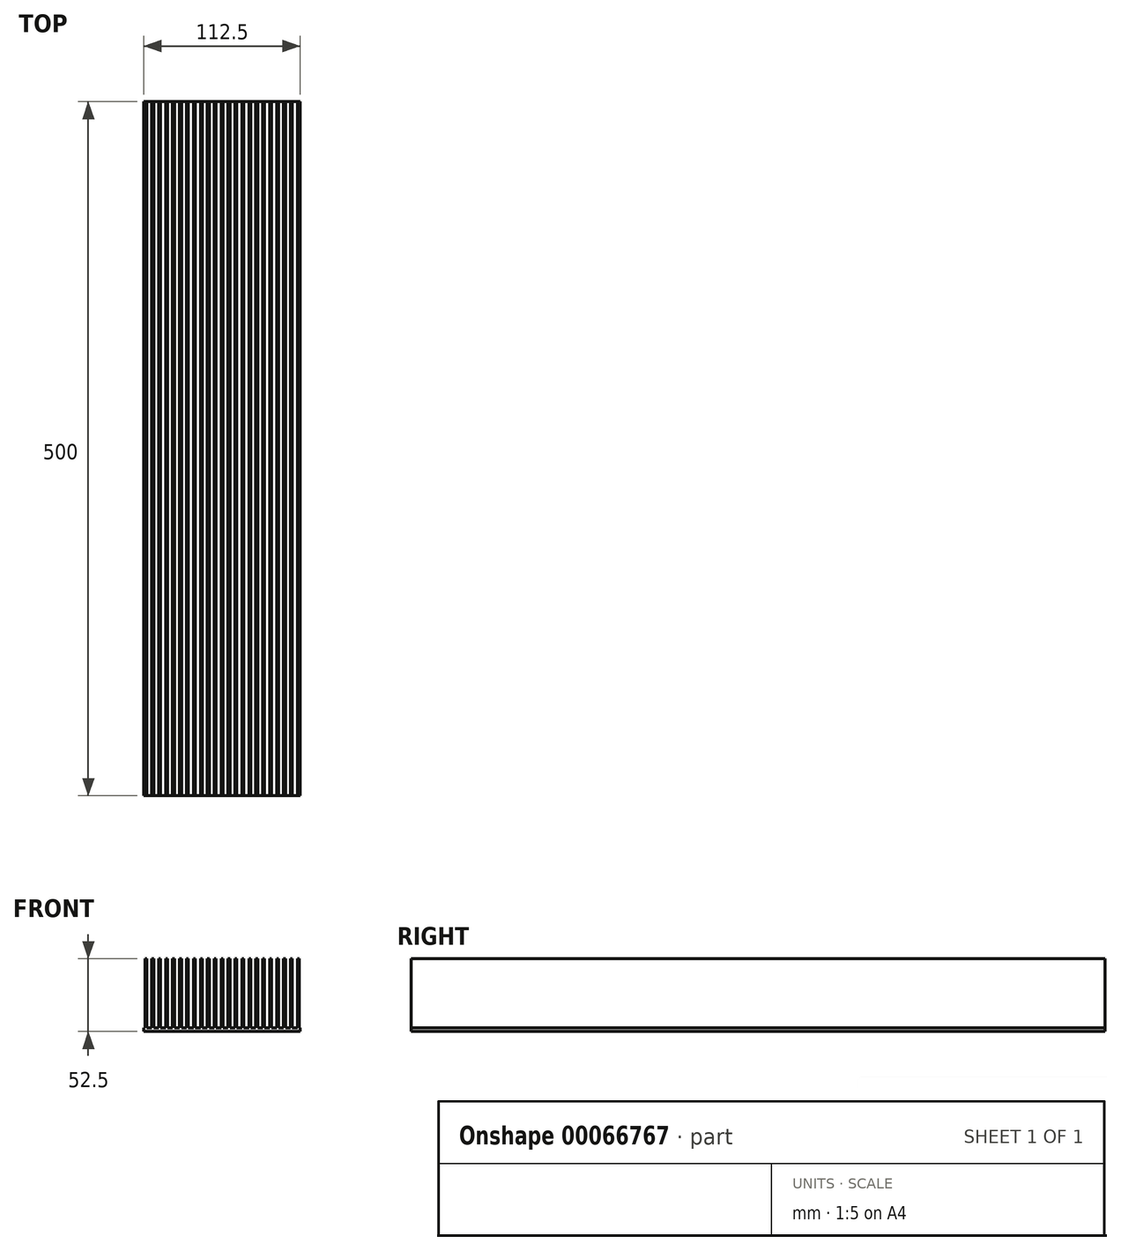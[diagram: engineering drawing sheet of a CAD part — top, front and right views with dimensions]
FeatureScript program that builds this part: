
annotation { "Feature Type Name" : "Feature", "Feature Type Description" : "" }
export const myFeature = defineFeature(function(context is Context, id is Id, definition is map)
    precondition{}
    {
        {
            var Q0;
            Q0=qCreatedBy(makeId("Front.planeOp"),FACE);
            var sketch = newSketch(context, id + "F0", { "sketchPlane" : qUnion([Q0])});
            skLineSegment(sketch, "E0", {"start": v(56.25, 1) * mm, "end": v(56.25, 3.5) * mm});
            skLineSegment(sketch, "E1", {"start": v(56.25, 3.5) * mm, "end": v(55.75, 3.5) * mm});
            skLineSegment(sketch, "E2", {"start": v(55.75, 3.5) * mm, "end": v(55.75, 53.5) * mm});
            skLineSegment(sketch, "E3", {"start": v(55.75, 53.5) * mm, "end": v(54.4, 53.5) * mm});
            skLineSegment(sketch, "E4", {"start": v(54.4, 53.5) * mm, "end": v(54.4, 3.5) * mm});
            skLineSegment(sketch, "E5", {"start": v(0, 1) * mm, "end": v(-56.25, 1) * mm});
            skLineSegment(sketch, "E6", {"start": v(-56.25, 1) * mm, "end": v(-56.25, 3.5) * mm});
            skLineSegment(sketch, "E7", {"start": v(-56.25, 3.5) * mm, "end": v(-52.25, 3.5) * mm});
            skLineSegment(sketch, "E8", {"start": v(-52.25, 3.5) * mm, "end": v(-52.25, 55.1) * mm, "construction": true});
            skLineSegment(sketch, "E9", {"start": v(-52.25, 3.5) * mm, "end": v(54.4, 3.5) * mm});
            skLineSegment(sketch, "E10.1.0.0", {"start": v(50.75, 53.5) * mm, "end": v(49.4, 53.5) * mm});
            skLineSegment(sketch, "E10.1.0.1", {"start": v(50.75, 3.5) * mm, "end": v(50.75, 53.5) * mm});
            skLineSegment(sketch, "E10.1.0.2", {"start": v(49.4, 53.5) * mm, "end": v(49.4, 3.5) * mm});
            skLineSegment(sketch, "E10.2.0.0", {"start": v(45.75, 53.5) * mm, "end": v(44.4, 53.5) * mm});
            skLineSegment(sketch, "E10.2.0.1", {"start": v(45.75, 3.5) * mm, "end": v(45.75, 53.5) * mm});
            skLineSegment(sketch, "E10.2.0.2", {"start": v(44.4, 53.5) * mm, "end": v(44.4, 3.5) * mm});
            skLineSegment(sketch, "E10.3.0.0", {"start": v(40.75, 53.5) * mm, "end": v(39.4, 53.5) * mm});
            skLineSegment(sketch, "E10.3.0.1", {"start": v(40.75, 3.5) * mm, "end": v(40.75, 53.5) * mm});
            skLineSegment(sketch, "E10.3.0.2", {"start": v(39.4, 53.5) * mm, "end": v(39.4, 3.5) * mm});
            skLineSegment(sketch, "E10.4.0.0", {"start": v(35.75, 53.5) * mm, "end": v(34.4, 53.5) * mm});
            skLineSegment(sketch, "E10.4.0.1", {"start": v(35.75, 3.5) * mm, "end": v(35.75, 53.5) * mm});
            skLineSegment(sketch, "E10.4.0.2", {"start": v(34.4, 53.5) * mm, "end": v(34.4, 3.5) * mm});
            skLineSegment(sketch, "E10.5.0.0", {"start": v(30.75, 53.5) * mm, "end": v(29.4, 53.5) * mm});
            skLineSegment(sketch, "E10.5.0.1", {"start": v(30.75, 3.5) * mm, "end": v(30.75, 53.5) * mm});
            skLineSegment(sketch, "E10.5.0.2", {"start": v(29.4, 53.5) * mm, "end": v(29.4, 3.5) * mm});
            skLineSegment(sketch, "E10.6.0.0", {"start": v(25.75, 53.5) * mm, "end": v(24.4, 53.5) * mm});
            skLineSegment(sketch, "E10.6.0.1", {"start": v(25.75, 3.5) * mm, "end": v(25.75, 53.5) * mm});
            skLineSegment(sketch, "E10.6.0.2", {"start": v(24.4, 53.5) * mm, "end": v(24.4, 3.5) * mm});
            skLineSegment(sketch, "E10.7.0.0", {"start": v(20.75, 53.5) * mm, "end": v(19.4, 53.5) * mm});
            skLineSegment(sketch, "E10.7.0.1", {"start": v(20.75, 3.5) * mm, "end": v(20.75, 53.5) * mm});
            skLineSegment(sketch, "E10.7.0.2", {"start": v(19.4, 53.5) * mm, "end": v(19.4, 3.5) * mm});
            skLineSegment(sketch, "E10.8.0.0", {"start": v(15.75, 53.5) * mm, "end": v(14.4, 53.5) * mm});
            skLineSegment(sketch, "E10.8.0.1", {"start": v(15.75, 3.5) * mm, "end": v(15.75, 53.5) * mm});
            skLineSegment(sketch, "E10.8.0.2", {"start": v(14.4, 53.5) * mm, "end": v(14.4, 3.5) * mm});
            skLineSegment(sketch, "E10.9.0.0", {"start": v(10.75, 53.5) * mm, "end": v(9.4, 53.5) * mm});
            skLineSegment(sketch, "E10.9.0.1", {"start": v(10.75, 3.5) * mm, "end": v(10.75, 53.5) * mm});
            skLineSegment(sketch, "E10.9.0.2", {"start": v(9.4, 53.5) * mm, "end": v(9.4, 3.5) * mm});
            skLineSegment(sketch, "E10.10.0.0", {"start": v(5.75, 53.5) * mm, "end": v(4.4, 53.5) * mm});
            skLineSegment(sketch, "E10.10.0.1", {"start": v(5.75, 3.5) * mm, "end": v(5.75, 53.5) * mm});
            skLineSegment(sketch, "E10.10.0.2", {"start": v(4.4, 53.5) * mm, "end": v(4.4, 3.5) * mm});
            skLineSegment(sketch, "E10.11.0.0", {"start": v(0.75, 53.5) * mm, "end": v(-0.6, 53.5) * mm});
            skLineSegment(sketch, "E10.11.0.1", {"start": v(0.75, 3.5) * mm, "end": v(0.75, 53.5) * mm});
            skLineSegment(sketch, "E10.11.0.2", {"start": v(-0.6, 53.5) * mm, "end": v(-0.6, 3.5) * mm});
            skLineSegment(sketch, "E10.12.0.0", {"start": v(-4.25, 53.5) * mm, "end": v(-5.6, 53.5) * mm});
            skLineSegment(sketch, "E10.12.0.1", {"start": v(-4.25, 3.5) * mm, "end": v(-4.25, 53.5) * mm});
            skLineSegment(sketch, "E10.12.0.2", {"start": v(-5.6, 53.5) * mm, "end": v(-5.6, 3.5) * mm});
            skLineSegment(sketch, "E10.13.0.0", {"start": v(-9.25, 53.5) * mm, "end": v(-10.6, 53.5) * mm});
            skLineSegment(sketch, "E10.13.0.1", {"start": v(-9.25, 3.5) * mm, "end": v(-9.25, 53.5) * mm});
            skLineSegment(sketch, "E10.13.0.2", {"start": v(-10.6, 53.5) * mm, "end": v(-10.6, 3.5) * mm});
            skLineSegment(sketch, "E10.14.0.0", {"start": v(-14.25, 53.5) * mm, "end": v(-15.6, 53.5) * mm});
            skLineSegment(sketch, "E10.14.0.1", {"start": v(-14.25, 3.5) * mm, "end": v(-14.25, 53.5) * mm});
            skLineSegment(sketch, "E10.14.0.2", {"start": v(-15.6, 53.5) * mm, "end": v(-15.6, 3.5) * mm});
            skLineSegment(sketch, "E10.15.0.0", {"start": v(-19.25, 53.5) * mm, "end": v(-20.6, 53.5) * mm});
            skLineSegment(sketch, "E10.15.0.1", {"start": v(-19.25, 3.5) * mm, "end": v(-19.25, 53.5) * mm});
            skLineSegment(sketch, "E10.15.0.2", {"start": v(-20.6, 53.5) * mm, "end": v(-20.6, 3.5) * mm});
            skLineSegment(sketch, "E10.16.0.0", {"start": v(-24.25, 53.5) * mm, "end": v(-25.6, 53.5) * mm});
            skLineSegment(sketch, "E10.16.0.1", {"start": v(-24.25, 3.5) * mm, "end": v(-24.25, 53.5) * mm});
            skLineSegment(sketch, "E10.16.0.2", {"start": v(-25.6, 53.5) * mm, "end": v(-25.6, 3.5) * mm});
            skLineSegment(sketch, "E10.17.0.0", {"start": v(-29.25, 53.5) * mm, "end": v(-30.6, 53.5) * mm});
            skLineSegment(sketch, "E10.17.0.1", {"start": v(-29.25, 3.5) * mm, "end": v(-29.25, 53.5) * mm});
            skLineSegment(sketch, "E10.17.0.2", {"start": v(-30.6, 53.5) * mm, "end": v(-30.6, 3.5) * mm});
            skLineSegment(sketch, "E10.direction1", {"start": v(54.4, 53.5) * mm, "end": v(49.4, 53.5) * mm, "construction": true});
            skLineSegment(sketch, "E11.0.18.0", {"start": v(-34.25, 53.5) * mm, "end": v(-35.6, 53.5) * mm});
            skLineSegment(sketch, "E11.3.18.0", {"start": v(-34.25, 3.5) * mm, "end": v(-34.25, 53.5) * mm});
            skLineSegment(sketch, "E11.6.18.0", {"start": v(-35.6, 53.5) * mm, "end": v(-35.6, 3.5) * mm});
            skLineSegment(sketch, "E11.0.19.0", {"start": v(-39.25, 53.5) * mm, "end": v(-40.6, 53.5) * mm});
            skLineSegment(sketch, "E11.3.19.0", {"start": v(-39.25, 3.5) * mm, "end": v(-39.25, 53.5) * mm});
            skLineSegment(sketch, "E11.6.19.0", {"start": v(-40.6, 53.5) * mm, "end": v(-40.6, 3.5) * mm});
            skLineSegment(sketch, "E12.0.20.0", {"start": v(-44.25, 53.5) * mm, "end": v(-45.6, 53.5) * mm});
            skLineSegment(sketch, "E12.3.20.0", {"start": v(-44.25, 3.5) * mm, "end": v(-44.25, 53.5) * mm});
            skLineSegment(sketch, "E12.6.20.0", {"start": v(-45.6, 53.5) * mm, "end": v(-45.6, 3.5) * mm});
            skLineSegment(sketch, "E12.0.21.0", {"start": v(-49.25, 53.5) * mm, "end": v(-50.6, 53.5) * mm});
            skLineSegment(sketch, "E12.3.21.0", {"start": v(-49.25, 3.5) * mm, "end": v(-49.25, 53.5) * mm});
            skLineSegment(sketch, "E12.6.21.0", {"start": v(-50.6, 53.5) * mm, "end": v(-50.6, 3.5) * mm});
            skLineSegment(sketch, "E13.0.22.0", {"start": v(-54.25, 53.5) * mm, "end": v(-55.6, 53.5) * mm});
            skLineSegment(sketch, "E13.3.22.0", {"start": v(-54.25, 3.5) * mm, "end": v(-54.25, 53.5) * mm});
            skLineSegment(sketch, "E13.6.22.0", {"start": v(-55.6, 53.5) * mm, "end": v(-55.6, 3.5) * mm});
            skLineSegment(sketch, "E14", {"start": v(56.25, 1) * mm, "end": v(0, 1) * mm});
            skSolve(sketch);
        }
        {
            var Q0;
            Q0=qSketchRegion(id+"F0",true);
            extrude(context, id + "F1", {"entities" : qUnion([Q0]), "depth" : 500 * mm});
        }
    });
